# Revit family: Camera-Security-iPRO-2MP-Indoor-PTZ-Network-WV-U6130X_B6130X-SeriesX
name_source: partatom
category: Security Devices
units: mm (PartAtom-declared; Revit-internal decimal feet)

## family parameters
Cut with Voids When Loaded = No
Host = Face
Maintain Annotation Orientation = No
OmniClass Number = 23.85.10.14.11
OmniClass Title = Cameras
Part Type = Normal
Room Calculation Point = No
Round Connector Dimension = Use Radius
Shared = No

## types (4) — shared parameters
Alarm Input Or Output Specification = ALARM IN 1 (Alarm input 1/ Black & white input/ Auto time adjustment input) (x1) ALARM IN 2 (Alarm input 2/ ALARM OUT) (x1),  ARM IN 3 (Alarm input 3/ AUX OUT) (x1)
Audio In = Yes
Audio Out = Yes
Communication Ports = 10Base-T / 100Base-TX, RJ-45
Date Last Modified = 2022/08/22
Day Or Night = Yes
Diameter = 4.606 "
Equipment Abbreviation = SC
Family Version = 1.0.0
Has POE = Yes
Height = 6.102 "
IP Or Analog = IP
Indoor Or Outdoor = Indoor
Manufacturer = i-PRO Co., Ltd.
Minimum Illumination = 0.015 lx
Model Disclaimer = Contact i-PRO for more information
Mounting Positions = Mount Dependent or Surface Mount
Operational Humidity = 10 to 90 % (no condensation)
Operational Temperature = -10 °C to +50 °C (+14 °F to +122 °F)
Pan Max = 350.00°
Pan Min = 0.00°
Panning Range = 0 to +350
Product Material = Paint - i-Pro White
Provide Feedback = https://i-pro.com
Regulatory Compliance = UL (UL62368-1), c-UL (CSA C22.2 No.62368-1), CE, IEC62368-1, FCC (Part15 ClassA), ICES-003 Issue 7 ClassA, EN55032 ClassA, EN55035
Storage Temperature = -30 ℃ to +60 ℃(-22°F to 68°F)
Tilt Max = 90.00°
Tilt Min = -30.00°
Tilting Range = -30 to +90
URL = https://i-pro.com
Vandal Resistant = No
Weight = 1.20 kgf
Wide Dynamic Range = Yes
z Const Pan Handle Length = 27.559 "
z Const Tilt Base Length = 9.843 "
z Const Tilt Base2 Length = 19.685 "
z Const Tilt Handle Length = 14.173 "
z Const Yaw Base Length = 10.236 "
z Const Yaw Base2 Length = 17.323 "
z Const Yaw Handle Length = 9.252 "
z VV Origin Height Offset = 2.972 "
zero-valued in all types: Default Elevation

## per-type parameters (varying)
| type | Angle Of View | Description | HFOV Max 169 | HFOV Max 43 | HFOV Min 169 | HFOV Min 43 | Part Description | Product Documentation Link | Product Page URL | VFOV Max 169 | VFOV Max 43 | VFOV Min 169 | VFOV Min 43 | z VV Viewpoint Depth Max | z VV Viewpoint Depth Min |
| WV-U61301-Z1 | 62 | Security Camera, 2MP 10x Indoor PTZ Network Camera, WV-U61301-Z1 | 62.00° | 48.00° | 6.70° | 5.10° | Security Camera, 2MP 10x Indoor PTZ Network Camera, WV-U61301-Z1 |  | https://cwc.i-pro.com | 37.00° | 37.00° | 3.80° | 3.80° | 1.701 " | 1.701 " |
| WV-U61301-Z2 | 77 | Security Camera, 2MP 21x Indoor PTZ Network Camera, WV-U61301-Z2 | 77.00° | 58.00° | 3.70° | 2.80° | Security Camera, 2MP 21x Indoor PTZ Network Camera, WV-U61301-Z2 | https://bizpartner.panasonic.net | https://i-pro.com | 44.00° | 44.00° | 2.20° | 2.20° | 1.687 " | 1.687 " |
| WV-B61301-Z1 | 62 | Security Camera, 2MP 10x Indoor PTZ Network Camera, WV-B61301-Z1 | 62.00° | 48.00° | 6.70° | 5.10° | Security Camera, 2MP 10x Indoor PTZ Network Camera, WV-B61301-Z1 |  | https://cwc.i-pro.com | 37.00° | 37.00° | 3.80° | 3.80° | 1.701 " | 1.701 " |
| WV-B61301-Z2 | 77 | Security Camera, 2MP 21x Indoor PTZ Network  Camera, WV-B61301-Z2 | 77.00° | 58.00° | 3.70° | 2.80° | Security Camera, 2MP 21x Indoor PTZ Network  Camera, WV-B61301-Z2 | https://cwc.i-pro.comhttps: | https://cwc.i-pro.com | 44.00° | 44.00° | 2.20° | 2.20° | 1.687 " | 1.687 " |

note: column(s) folded — value = type name in every type: Model, Part Number

## geometry (parser evidence)
native form markers: Blend x2, Sweep x7
no freeform markers — native parametric forms only
